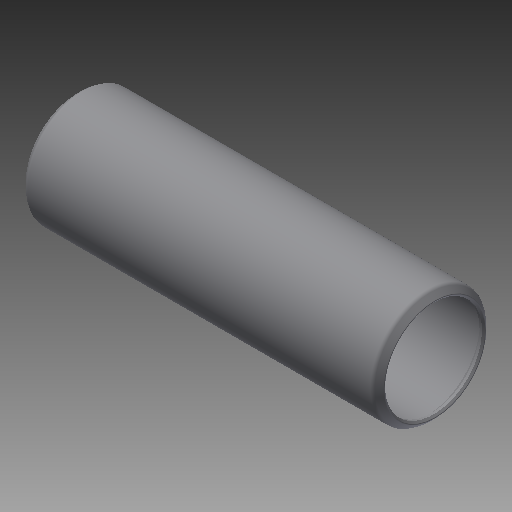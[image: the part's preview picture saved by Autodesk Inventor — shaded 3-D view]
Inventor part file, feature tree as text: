
AUTODESK INVENTOR PART (.ipt)
format: ipt  version: 2018 (Build 220112000, 112)  size: 166,912 bytes
history: native  units: in
note: dims shown in document units (in); Inventor stores cm internally (conversion verified against a paired STEP export)
features: other x42, revolve x1, sketch x1
ambient origin geometry x8: Origin, YZ Plane, XZ Plane, XY Plane, X Axis, Y Axis, Z Axis, Center Point
bodies: Solid1 (feature_tree)
feature tree (44):
  revolve  "Revolution1"  [1 undecoded]
  other  "cp1_XY"
  other  "cp1_YZ"
  other  "cp1_ZX"
  other  "cp1_X"
  other  "cp1_Y"
  other  "cp1_Z"
  other  "cp1_Center"
  other  "cp2_XY"
  other  "cp2_YZ"
  other  "cp2_ZX"
  other  "cp2_X"
  other  "cp2_Y"
  other  "cp2_Z"
  other  "cp2_Center"
  other  "cp3_XY"
  other  "cp3_YZ"
  other  "cp3_ZX"
  other  "cp3_X"
  other  "cp3_Y"
  other  "cp3_Z"
  other  "cp3_Center"
  other  "cp4_XY"
  other  "cp4_YZ"
  other  "cp4_ZX"
  other  "cp4_X"
  other  "cp4_Y"
  other  "cp4_Z"
  other  "cp4_Center"
  other  "tube_front_XY"
  other  "tube_front_YZ"
  other  "tube_front_ZX"
  other  "tube_front_X"
  other  "tube_front_Y"
  other  "tube_front_Z"
  other  "tube_front_Center"
  other  "tube_rear_XY"
  other  "tube_rear_YZ"
  other  "tube_rear_ZX"
  other  "tube_rear_X"
  other  "tube_rear_Y"
  other  "tube_rear_Z"
  other  "tube_rear_Center"
  sketch  "Sketch_1"  dims[d0=360.0deg]
note: 1 required parameter value undecoded (feature->parameter linkage not recoverable at this tier; creation-order binding heuristic only, values carry confidence <= 0.55)
